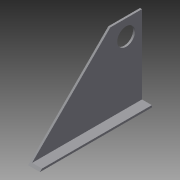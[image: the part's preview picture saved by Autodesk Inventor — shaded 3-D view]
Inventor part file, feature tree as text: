
AUTODESK INVENTOR PART (.ipt)
format: ipt  version: 2013 (Build 170138000, 138)  size: 92,160 bytes
history: native  units: in
note: dims shown in document units (in); Inventor stores cm internally (conversion verified against a paired STEP export)
features: extrude x2, sketch x2
ambient origin geometry x8: Origin, YZ Plane, XZ Plane, XY Plane, X Axis, Y Axis, Z Axis, Center Point
bodies: Solid1 (feature_tree)
feature tree (4):
  extrude  "Extrusion1"  TaperAngle=0.0deg  [1 undecoded]
  extrude  "Extrusion2"  Depth=1.0in
  sketch  "Sketch1"  dims[d0=4.063in d1=0.0in]
  sketch  "Sketch2"  dims[d2=1.125in d3=1.0in d4=0.0in d5=1.0in d6=90.0deg d7=1.0in d8=90.0deg d9=135.0deg d10=0.125in d11=0.0in d12=0.125in d13=90.0deg d14=0.625in d15=0.0in]
note: 1 required parameter value undecoded (feature->parameter linkage not recoverable at this tier; creation-order binding heuristic only, values carry confidence <= 0.55)
